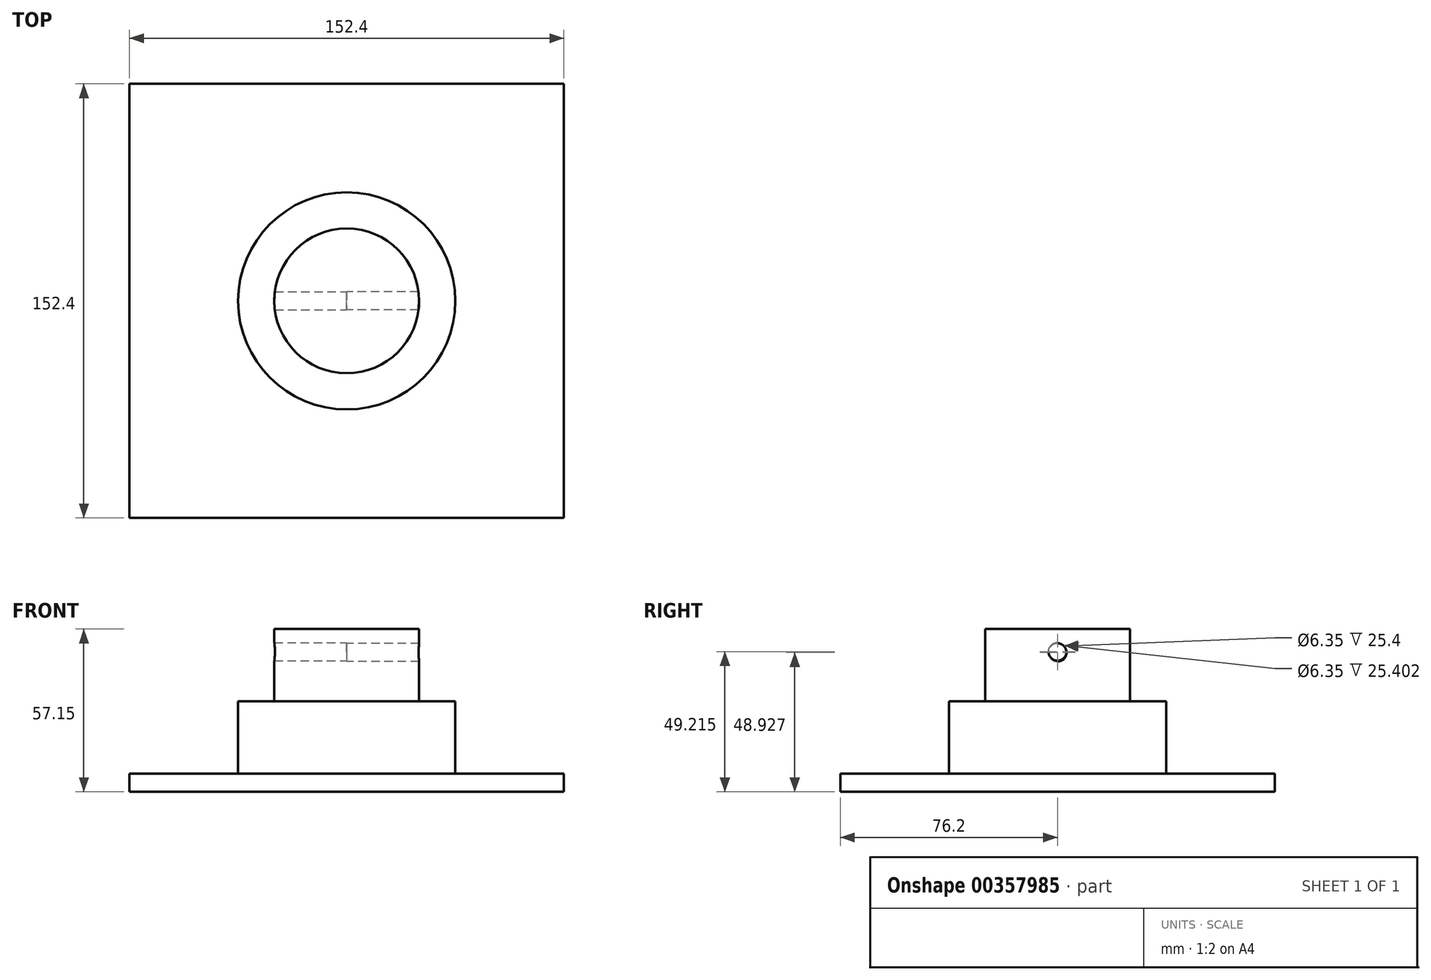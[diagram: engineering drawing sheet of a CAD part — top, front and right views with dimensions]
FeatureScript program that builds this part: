
annotation { "Feature Type Name" : "Feature", "Feature Type Description" : "" }
export const myFeature = defineFeature(function(context is Context, id is Id, definition is map)
    precondition{}
    {
        {
            var Q0;
            Q0=qCreatedBy(makeId("Top.planeOp"),FACE);
            var sketch = newSketch(context, id + "F0", { "sketchPlane" : qUnion([Q0])});
            skLineSegment(sketch, "E0.bottom", {"start": v(76.2, 76.2) * mm, "end": v(-76.2, 76.2) * mm});
            skLineSegment(sketch, "E0.top", {"start": v(76.2, -76.2) * mm, "end": v(-76.2, -76.2) * mm});
            skLineSegment(sketch, "E0.left", {"start": v(76.2, 76.2) * mm, "end": v(76.2, -76.2) * mm});
            skLineSegment(sketch, "E0.right", {"start": v(-76.2, 76.2) * mm, "end": v(-76.2, -76.2) * mm});
            skPoint(sketch, "E0.middle", {"position": v(0, 0) * mm});
            skSolve(sketch);
        }
        {
            var Q0;
            Q0=makeQuery(id+"F0.imprint","IMPRINT",FACE,{"disambiguationData":[TD([[makeQuery(id+"F0.imprint","IMPRINT",EDGE,{"derivedFrom":sQuery(id+"F0.wireOp",EDGE,"E0.bottom")}),1.0]])]});
            extrude(context, id + "F1", {"entities" : qUnion([Q0]), "depth" : 6.35 * mm});
        }
        {
            var Q0;
            Q0=makeQuery(id+"F1.opExtrude","CAP_FACE",FACE,{"disambiguationData":[OSD([sQuery(id+"F0.wireOp",EDGE,"E0.bottom"),sQuery(id+"F0.wireOp",EDGE,"E0.top"),sQuery(id+"F0.wireOp",EDGE,"E0.left"),sQuery(id+"F0.wireOp",EDGE,"E0.right")])],"isStart":false});
            var sketch = newSketch(context, id + "F2", { "sketchPlane" : qUnion([Q0])});
            skCircle(sketch, "E1", {"center": v(0, 0) * mm, "radius": 38.1 * mm});
            skSolve(sketch);
        }
        {
            var Q0;
            Q0=makeQuery(id+"F2.imprint","IMPRINT",FACE,{"disambiguationData":[TD([[makeQuery(id+"F2.imprint","IMPRINT",EDGE,{"derivedFrom":sQuery(id+"F2.wireOp",EDGE,"E1")}),1.0]])]});
            extrude(context, id + "F3", {"entities" : qUnion([Q0]), "operationType" : NewBodyOperationType.ADD, "depth" : 25.4 * mm});
        }
        {
            var Q0;
            Q0=makeQuery(id+"F3.opExtrude","CAP_FACE",FACE,{"disambiguationData":[OSD([sQuery(id+"F2.wireOp",EDGE,"E1")])],"isStart":false});
            var sketch = newSketch(context, id + "F4", { "sketchPlane" : qUnion([Q0])});
            skCircle(sketch, "E2", {"center": v(0, 0) * mm, "radius": 25.4 * mm});
            skSolve(sketch);
        }
        {
            var Q0;
            Q0=makeQuery(id+"F4.imprint","IMPRINT",FACE,{"disambiguationData":[TD([[makeQuery(id+"F4.imprint","IMPRINT",EDGE,{"derivedFrom":sQuery(id+"F4.wireOp",EDGE,"E2")}),1.0]])]});
            extrude(context, id + "F5", {"entities" : qUnion([Q0]), "operationType" : NewBodyOperationType.ADD, "depth" : 25.4 * mm});
        }
        {
            var Q0;
            Q0=qCreatedBy(makeId("Right.planeOp"),FACE);
            var sketch = newSketch(context, id + "F6", { "sketchPlane" : qUnion([Q0])});
            skCircle(sketch, "E3", {"center": v(0, 48.93) * mm, "radius": 6.32 * mm});
            skSolve(sketch);
        }
        {
            var Q0;
            Q0=sQuery(id+"F6.wireOp",VERTEX,"E3.center");
            var Q1;
            Q1=makeQuery(id+"F1.opExtrude","SWEPT_BODY",BODY,{"disambiguationData":[OSD([sQuery(id+"F0.wireOp",EDGE,"E0.bottom"),sQuery(id+"F0.wireOp",EDGE,"E0.top"),sQuery(id+"F0.wireOp",EDGE,"E0.left"),sQuery(id+"F0.wireOp",EDGE,"E0.right")])]});
            hole(context, id + "F7", {"style" : HoleStyle.SIMPLE, "endStyle" : HoleEndStyle.THROUGH, "oppositeDirection" : true, "holeDiameter" : 6.35 * mm, "isTappedThrough" : true, "tappedDepth" : 12.7 * mm, "tapClearance" : 3, "startFromSketch" : true, "locations" : qUnion([Q0]), "scope" : qUnion([Q1])});
        }
        {
            var Q0;
            Q0=qCreatedBy(makeId("Right.planeOp"),FACE);
            var sketch = newSketch(context, id + "F8", { "sketchPlane" : qUnion([Q0])});
            skCircle(sketch, "E4", {"center": v(0, 49.21) * mm, "radius": 5.6 * mm});
            skSolve(sketch);
        }
        {
            var Q0;
            Q0=sQuery(id+"F8.wireOp",VERTEX,"E4.center");
            var Q1;
            Q1=makeQuery(id+"F1.opExtrude","SWEPT_BODY",BODY,{"disambiguationData":[OSD([sQuery(id+"F0.wireOp",EDGE,"E0.bottom"),sQuery(id+"F0.wireOp",EDGE,"E0.top"),sQuery(id+"F0.wireOp",EDGE,"E0.left"),sQuery(id+"F0.wireOp",EDGE,"E0.right")])]});
            hole(context, id + "F9", {"style" : HoleStyle.SIMPLE, "endStyle" : HoleEndStyle.THROUGH, "holeDiameter" : 6.35 * mm, "isTappedThrough" : true, "tappedDepth" : 12.7 * mm, "tapClearance" : 3, "startFromSketch" : true, "locations" : qUnion([Q0]), "scope" : qUnion([Q1])});
        }
    });
